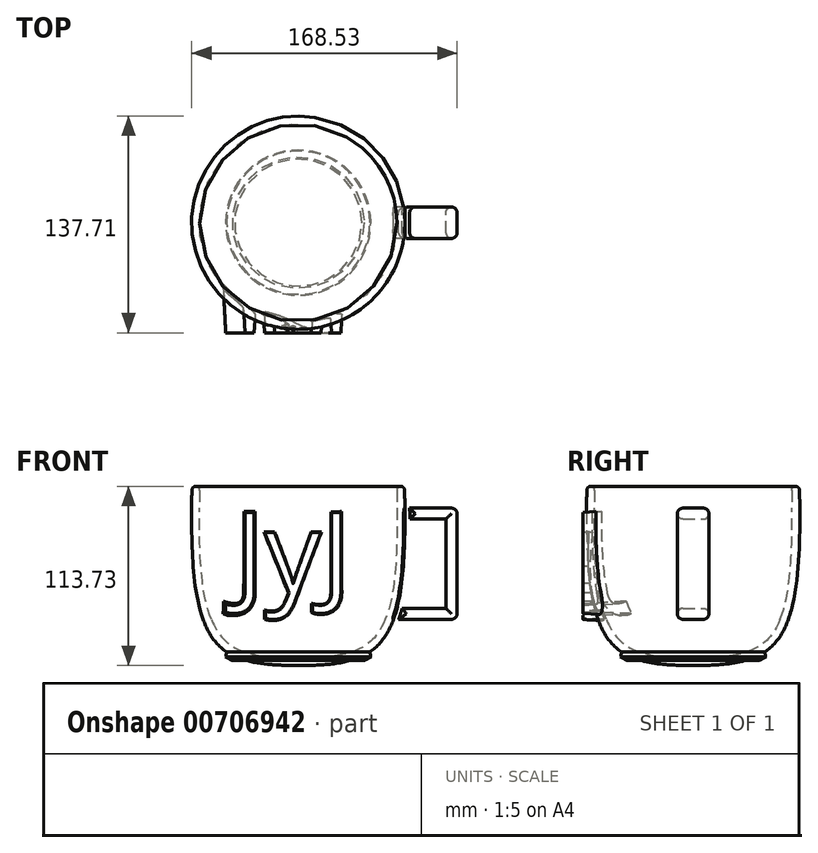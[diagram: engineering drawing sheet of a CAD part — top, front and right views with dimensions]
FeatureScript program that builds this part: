
annotation { "Feature Type Name" : "Feature", "Feature Type Description" : "" }
export const myFeature = defineFeature(function(context is Context, id is Id, definition is map)
    precondition{}
    {
        {
            var Q0;
            Q0=qCreatedBy(makeId("Front.planeOp"),FACE);
            var sketch = newSketch(context, id + "F0", { "sketchPlane" : qUnion([Q0])});
            skFitSpline(sketch, "E0", {"points": [v(67.44, 59.03) * mm, v(51.37, -46.7) * mm, v(-10.27, -60.15) * mm], "startDerivative": vector(3.7, -231.06) * mm, "endDerivative": vector(-166.56, 2.92) * mm});
            skFitSpline(sketch, "E1.0", {"points": [v(62.44, 58.95) * mm, v(62.6, 49.32) * mm, v(62.82, 34.93) * mm, v(62.54, 16.66) * mm, v(61.9, 3.64) * mm, v(60.7, -8.49) * mm, v(58.78, -19.48) * mm, v(56.53, -27.5) * mm, v(54.3, -33.11) * mm, v(52.42, -36.9) * mm, v(50.67, -39.67) * mm, v(49.16, -41.66) * mm, v(47.98, -43.04) * mm, v(46.73, -44.31) * mm, v(44.98, -45.89) * mm, v(42.61, -47.65) * mm, v(39.47, -49.45) * mm, v(34.89, -51.47) * mm, v(28.43, -53.34) * mm, v(19.7, -54.67) * mm, v(10.2, -55.25) * mm, v(0.18, -55.34) * mm, v(-6.72, -55.21) * mm, v(-10.19, -55.15) * mm]});
            skLineSegment(sketch, "E2", {"start": v(0, -24.66) * mm, "end": v(0, -73.6) * mm});
            skLineSegment(sketch, "E3", {"start": v(49.5, 53.43) * mm, "end": v(77.9, 53.43) * mm});
            skFitSpline(sketch, "E4", {"points": [v(45.46, -51.67) * mm, v(46.89, -64.64) * mm, v(40.42, -54.47) * mm], "startDerivative": vector(6.9, -37.22) * mm, "endDerivative": vector(-17.12, 32.05) * mm});
            skLineSegment(sketch, "E5.bottom", {"start": v(62.69, 39.6) * mm, "end": v(100.82, 39.6) * mm});
            skLineSegment(sketch, "E5.top", {"start": v(55.12, -31.01) * mm, "end": v(100.82, -31.01) * mm});
            skLineSegment(sketch, "E5.right", {"start": v(100.82, 39.6) * mm, "end": v(100.82, -31.01) * mm});
            skFitSpline(sketch, "E6.trimOffspring", {"points": [v(70.44, 59.08) * mm, v(70.6, 49.45) * mm, v(70.82, 34.98) * mm, v(70.54, 16.43) * mm, v(69.88, 3.08) * mm, v(68.63, -9.52) * mm, v(66.61, -21.18) * mm, v(64.16, -29.97) * mm, v(61.63, -36.35) * mm, v(59.41, -40.8) * mm, v(56.86, -44.85) * mm, v(54.42, -47.89) * mm, v(52.28, -50.09) * mm, v(50.01, -52.12) * mm, v(46.98, -54.37) * mm, v(43.07, -56.61) * mm, v(37.52, -59.06) * mm, v(30.06, -61.2) * mm, v(20.48, -62.64) * mm, v(10.44, -63.25) * mm, v(0.1, -63.34) * mm, v(-6.86, -63.21) * mm, v(-10.33, -63.15) * mm]});
            skLineSegment(sketch, "E7.0", {"start": v(62.69, 32.6) * mm, "end": v(62.71, 32.6) * mm});
            skLineSegment(sketch, "E8.0", {"start": v(93.82, 32.6) * mm, "end": v(93.82, -24.01) * mm});
            skLineSegment(sketch, "E9.trimOffspring", {"start": v(65.74, -24.01) * mm, "end": v(93.82, -24.01) * mm});
            skLineSegment(sketch, "E10.trimOffspring", {"start": v(70.71, 32.6) * mm, "end": v(93.82, 32.6) * mm});
            skSolve(sketch);
        }
        {
            var Q0;
            {var subQ0=sQuery(id+"F0.wireOp",EDGE,"E3");var subQ1=sQuery(id+"F0.wireOp",EDGE,"E0");var subQ2=makeQuery(id+"F0.imprint","INTERSECT",VERTEX,{"derivedFrom":[subQ1,subQ0]});Q0=makeQuery(id+"F0.imprint","IMPRINT",FACE,{"disambiguationData":[TD([[makeQuery(id+"F0.imprint","IMPRINT",EDGE,{"disambiguationData":[TD([[subQ2,-1.0]])],"derivedFrom":subQ1}),-1.0]])]});}
            var Q1;
            {var subQ0=sQuery(id+"F0.wireOp",EDGE,"E5.bottom");var subQ1=sQuery(id+"F0.wireOp",EDGE,"E0");var subQ2=makeQuery(id+"F0.imprint","INTERSECT",VERTEX,{"derivedFrom":[subQ1,subQ0]});Q1=makeQuery(id+"F0.imprint","IMPRINT",FACE,{"disambiguationData":[TD([[makeQuery(id+"F0.imprint","IMPRINT",EDGE,{"disambiguationData":[TD([[subQ2,-1.0]])],"derivedFrom":subQ1}),-1.0]])]});}
            var Q2;
            {var subQ0=sQuery(id+"F0.wireOp",EDGE,"E4");var subQ1=sQuery(id+"F0.wireOp",EDGE,"E0");var subQ9=makeQuery(id+"F0.imprint","INTERSECT",VERTEX,{"disambiguationData":[OD(0.0)],"derivedFrom":[subQ1,subQ0]});Q2=makeQuery(id+"F0.imprint","IMPRINT",FACE,{"disambiguationData":[TD([[makeQuery(id+"F0.imprint","IMPRINT",EDGE,{"disambiguationData":[TD([[subQ9,1.0]])],"derivedFrom":subQ1}),-1.0]])]});}
            var Q3;
            {var subQ0=sQuery(id+"F0.wireOp",EDGE,"E4");Q3=makeQuery(id+"F0.imprint","IMPRINT",FACE,{"disambiguationData":[TD([[makeQuery(id+"F0.imprint","IMPRINT",EDGE,{"derivedFrom":subQ0}),-1.0]])]});}
            var Q4;
            Q4=sQuery(id+"F0.wireOp",EDGE,"E2");
            revolve(context, id + "F1", {"surfaceOperationType" : NewSurfaceOperationType.NEW, "entities" : qUnion([Q0, Q1, Q2, Q3]), "axis" : qUnion([Q4]), "revolveType" : RevolveType.FULL});
        }
        {
            var Q0;
            {var subQ5=sQuery(id+"F0.wireOp",EDGE,"E5.right");Q0=makeQuery(id+"F0.imprint","IMPRINT",FACE,{"disambiguationData":[TD([[makeQuery(id+"F0.imprint","IMPRINT",EDGE,{"derivedFrom":subQ5}),-1.0]])]});}
            var Q1;
            {var subQ0=sQuery(id+"F0.wireOp",EDGE,"E5.bottom");var subQ1=sQuery(id+"F0.wireOp",EDGE,"E0");var subQ2=makeQuery(id+"F0.imprint","INTERSECT",VERTEX,{"derivedFrom":[subQ1,subQ0]});Q1=makeQuery(id+"F0.imprint","IMPRINT",FACE,{"disambiguationData":[TD([[makeQuery(id+"F0.imprint","IMPRINT",EDGE,{"disambiguationData":[TD([[subQ2,-1.0]])],"derivedFrom":subQ1}),-1.0]])]});}
            var Q2;
            {var subQ5=sQuery(id+"F0.wireOp",EDGE,"E5.left");Q2=makeQuery(id+"F0.imprint","IMPRINT",FACE,{"disambiguationData":[TD([[makeQuery(id+"F0.imprint","IMPRINT",EDGE,{"derivedFrom":subQ5}),1.0]])]});}
            extrude(context, id + "F2", {"entities" : qUnion([Q0, Q1, Q2]), "operationType" : NewBodyOperationType.ADD, "endBound" : BoundingType.SYMMETRIC, "depth" : 20 * mm, "offsetDistance" : 25 * mm});
        }
        {
            var Q0;
            Q0=makeQuery(id+"F2.opExtrude","CAP_EDGE",EDGE,{"disambiguationData":[OSD([sQuery(id+"F0.wireOp",EDGE,"E5.bottom")])],"isStart":false});
            var Q1;
            Q1=makeQuery(id+"F2.opExtrude","CAP_EDGE",EDGE,{"disambiguationData":[OSD([sQuery(id+"F0.wireOp",EDGE,"E5.bottom")])],"isStart":true});
            var Q2;
            Q2=makeQuery(id+"F2.opExtrude","CAP_EDGE",EDGE,{"disambiguationData":[OSD([sQuery(id+"F0.wireOp",EDGE,"E10.trimOffspring")])],"isStart":true});
            var Q3;
            Q3=makeQuery(id+"F2.opExtrude","CAP_EDGE",EDGE,{"disambiguationData":[OSD([sQuery(id+"F0.wireOp",EDGE,"E10.trimOffspring")])],"isStart":false});
            var Q4;
            Q4=makeQuery(id+"F2.opExtrude","CAP_EDGE",EDGE,{"disambiguationData":[OSD([sQuery(id+"F0.wireOp",EDGE,"E9.trimOffspring")])],"isStart":false});
            var Q5;
            Q5=makeQuery(id+"F2.opExtrude","CAP_EDGE",EDGE,{"disambiguationData":[OSD([sQuery(id+"F0.wireOp",EDGE,"E9.trimOffspring")])],"isStart":true});
            var Q6;
            Q6=makeQuery(id+"F2.opExtrude","CAP_EDGE",EDGE,{"disambiguationData":[OSD([sQuery(id+"F0.wireOp",EDGE,"E6.trimOffspring")])],"isStart":true});
            var Q7;
            Q7=makeQuery(id+"F2.opExtrude","CAP_EDGE",EDGE,{"disambiguationData":[OSD([sQuery(id+"F0.wireOp",EDGE,"E6.trimOffspring")])],"isStart":false});
            var Q8;
            Q8=makeQuery(id+"F2.opExtrude","CAP_EDGE",EDGE,{"disambiguationData":[OSD([sQuery(id+"F0.wireOp",EDGE,"E8.0")])],"isStart":true});
            var Q9;
            Q9=makeQuery(id+"F2.opExtrude","CAP_EDGE",EDGE,{"disambiguationData":[OSD([sQuery(id+"F0.wireOp",EDGE,"E8.0")])],"isStart":false});
            var Q10;
            Q10=makeQuery(id+"F2.opExtrude","SWEPT_EDGE",EDGE,{"disambiguationData":[OSD([sQuery(id+"F0.wireOp",EDGE,"E5.bottom"),sQuery(id+"F0.wireOp",EDGE,"E5.right")])]});
            var Q11;
            Q11=makeQuery(id+"F2.opExtrude","SWEPT_EDGE",EDGE,{"disambiguationData":[OSD([sQuery(id+"F0.wireOp",EDGE,"E5.top"),sQuery(id+"F0.wireOp",EDGE,"E5.right")])]});
            var Q12;
            Q12=makeQuery(id+"F2.opExtrude","CAP_EDGE",EDGE,{"disambiguationData":[OSD([sQuery(id+"F0.wireOp",EDGE,"E5.right")])],"isStart":false});
            var Q13;
            Q13=makeQuery(id+"F2.opExtrude","CAP_EDGE",EDGE,{"disambiguationData":[OSD([sQuery(id+"F0.wireOp",EDGE,"E5.right")])],"isStart":true});
            var Q14;
            Q14=makeQuery(id+"F2.opExtrude","CAP_EDGE",EDGE,{"disambiguationData":[OSD([sQuery(id+"F0.wireOp",EDGE,"E5.top")])],"isStart":false});
            var Q15;
            Q15=makeQuery(id+"F2.opExtrude","CAP_EDGE",EDGE,{"disambiguationData":[OSD([sQuery(id+"F0.wireOp",EDGE,"E5.top")])],"isStart":true});
            fillet(context, id + "F3", {"entities" : qUnion([Q0, Q1, Q2, Q3, Q4, Q5, Q6, Q7, Q8, Q9, Q10, Q11, Q12, Q13, Q14, Q15]), "radius" : 3.5 * mm, "tangentPropagation" : true, "allowEdgeOverflow" : false});
        }
        {
            var Q0;
            Q0=makeQuery(id+"F1.opRevolve","SWEPT_FACE",FACE,{"disambiguationData":[OSD([sQuery(id+"F0.wireOp",EDGE,"E3")])]});
            fillet(context, id + "F4", {"entities" : qUnion([Q0]), "radius" : 2.5 * mm, "tangentPropagation" : true, "allowEdgeOverflow" : false});
        }
        {
            var Q0;
            Q0=qCreatedBy(makeId("Front.planeOp"),FACE);
            cPlane(context, id + "F5", {"entities" : qUnion([Q0]), "cplaneType" : CPlaneType.OFFSET, "offset" : 70 * mm, "width" : 150 * mm, "height" : 150 * mm});
        }
        {
            var Q0;
            Q0=qCreatedBy(id+"F5.planeOp",FACE);
            var sketch = newSketch(context, id + "F6", { "sketchPlane" : qUnion([Q0])});
            skText(sketch, "E11", { "text": "JyJ", "fontName": "OpenSans-Regular.ttf"});
            const initialGuessF6  = {"E11": [-0.04047, -0.01397, 1, 0, 0.05135]};
            skSetInitialGuess(sketch, initialGuessF6);
            skSolve(sketch);
        }
        {
            var Q0;
            Q0 = qSketchRegion(id + "F6", true);
            extrude(context, id + "F7", {"entities" : qUnion([Q0]), "endBound" : BoundingType.UP_TO_NEXT, "oppositeDirection" : true, "depth" : 25 * mm, "offsetDistance" : 25 * mm, "hasDraft" : true, "draftAngle" : 3 * degree});
        }
    });
